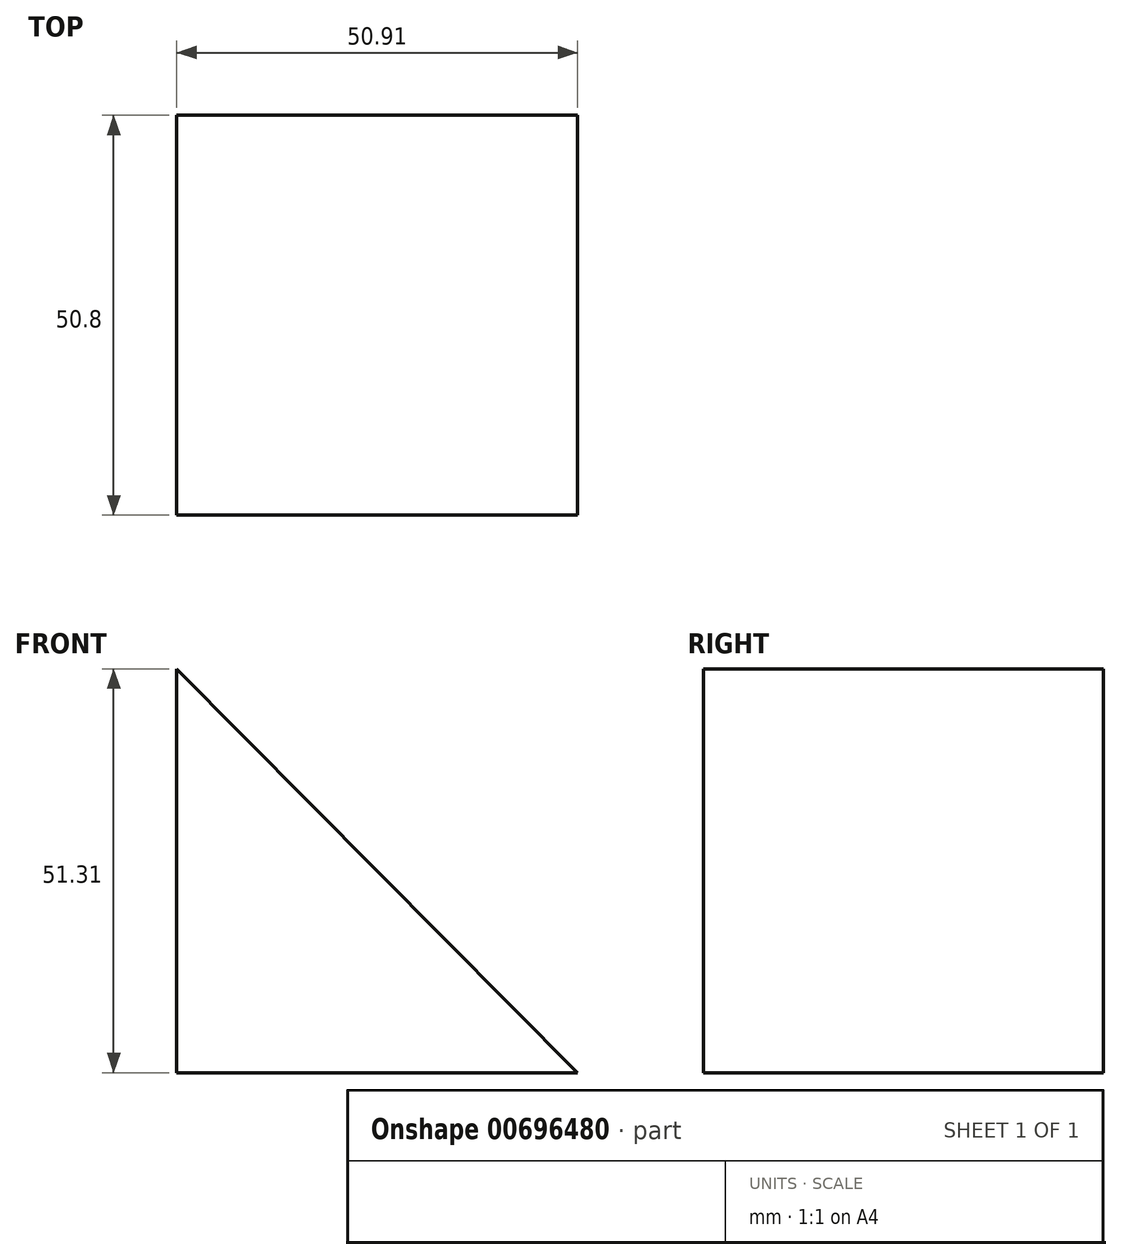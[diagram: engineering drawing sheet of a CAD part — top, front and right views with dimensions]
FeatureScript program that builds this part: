
annotation { "Feature Type Name" : "Feature", "Feature Type Description" : "" }
export const myFeature = defineFeature(function(context is Context, id is Id, definition is map)
    precondition{}
    {
        {
            var Q0;
            Q0=qCreatedBy(makeId("Front.planeOp"),FACE);
            var sketch = newSketch(context, id + "F0", { "sketchPlane" : qUnion([Q0])});
            skLineSegment(sketch, "E0", {"start": v(0, 0) * mm, "end": v(0, 51.3) * mm});
            skLineSegment(sketch, "E1", {"start": v(0, 0) * mm, "end": v(50.9, 0) * mm});
            skLineSegment(sketch, "E2", {"start": v(50.9, 0) * mm, "end": v(0, 51.3) * mm});
            skSolve(sketch);
        }
        {
            var Q0;
            Q0=makeQuery(id+"F0.imprint","IMPRINT",FACE,{"disambiguationData":[TD([[makeQuery(id+"F0.imprint","IMPRINT",EDGE,{"derivedFrom":sQuery(id+"F0.wireOp",EDGE,"E0")}),-1.0]])]});
            extrude(context, id + "F1", {"entities" : qUnion([Q0]), "depth" : 50.8 * mm, "offsetDistance" : 25.4 * mm});
        }
    });
